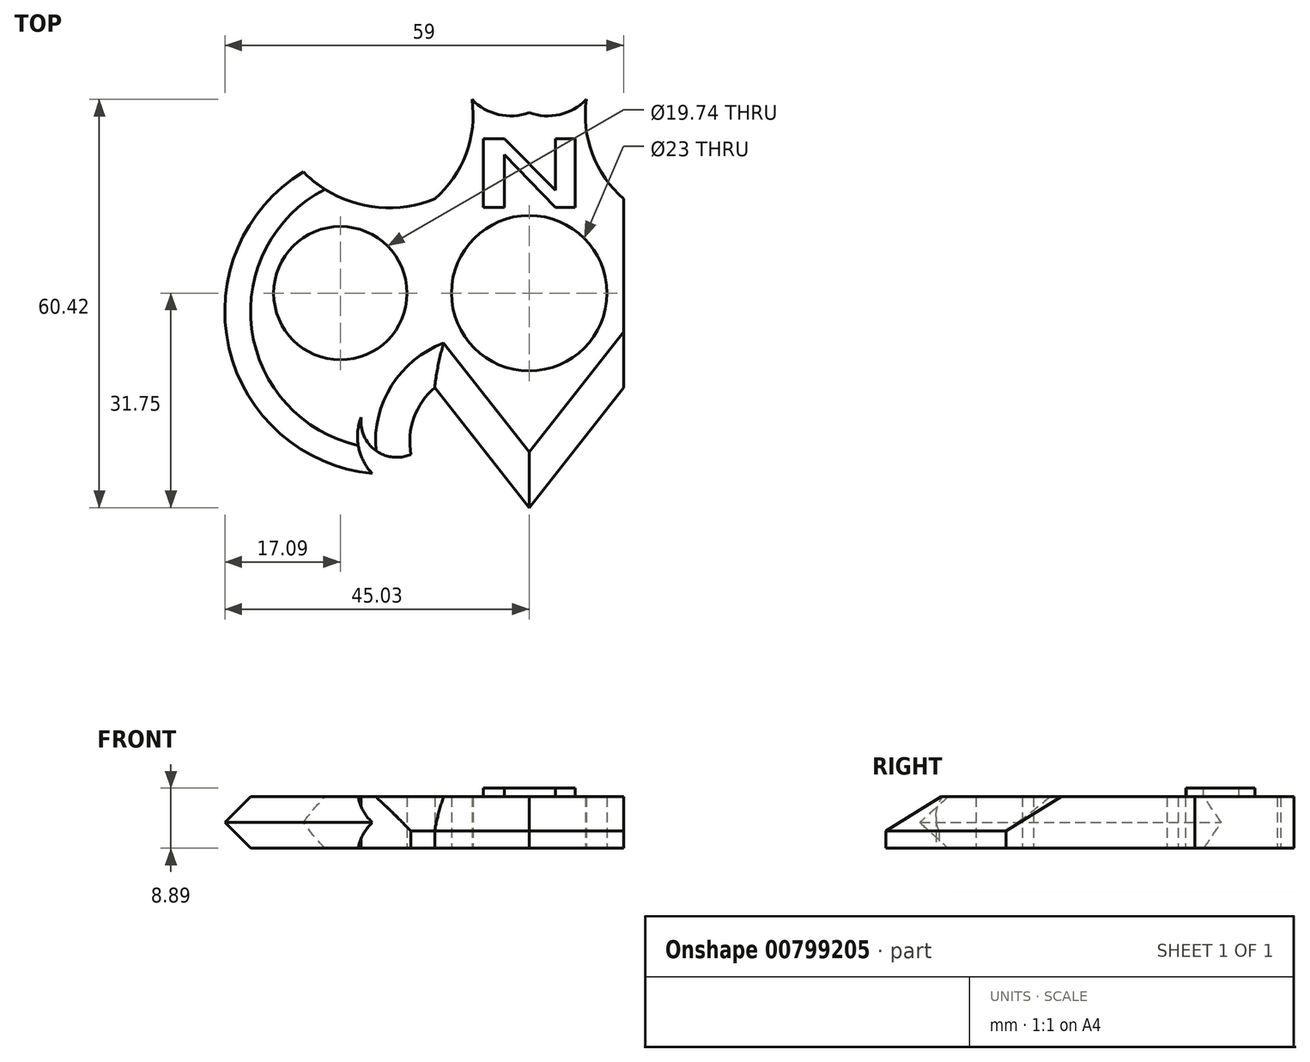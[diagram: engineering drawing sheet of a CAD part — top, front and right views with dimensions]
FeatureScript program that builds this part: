
annotation { "Feature Type Name" : "Feature", "Feature Type Description" : "" }
export const myFeature = defineFeature(function(context is Context, id is Id, definition is map)
    precondition{}
    {
        {
            var Q0;
            Q0=qCreatedBy(makeId("Top.planeOp"),FACE);
            var sketch = newSketch(context, id + "F0", { "sketchPlane" : qUnion([Q0])});
            skCircle(sketch, "E0", {"center": v(0, 0) * mm, "radius": 11.5 * mm});
            skLineSegment(sketch, "E1.bottom", {"start": v(13.97, -13.97) * mm, "end": v(-13.97, -13.97) * mm});
            skLineSegment(sketch, "E1.top", {"start": v(13.97, 13.97) * mm, "end": v(-13.97, 13.97) * mm});
            skLineSegment(sketch, "E1.left", {"start": v(13.97, -13.97) * mm, "end": v(13.97, 13.97) * mm});
            skLineSegment(sketch, "E1.right", {"start": v(-13.97, -13.97) * mm, "end": v(-13.97, 13.97) * mm});
            skArc(sketch, "E2", {"start": v(-34.3, 18.9) * mm, "mid": v(-24.93, 13.13) * mm, "end": v(-13.97, 13.97) * mm});
            skArc(sketch, "E3", {"start": v(-34.3, 18.9) * mm, "mid": v(-45.4, -9.38) * mm, "end": v(-21.46, -28.08) * mm});
            skLineSegment(sketch, "E4", {"start": v(-13.97, -13.97) * mm, "end": v(0, -31.75) * mm});
            skArc(sketch, "E5", {"start": v(-13.97, 13.97) * mm, "mid": v(-9.35, 20.62) * mm, "end": v(-8.45, 28.67) * mm});
            skArc(sketch, "E6", {"start": v(-8.45, 28.67) * mm, "mid": v(-4.52, 26.42) * mm, "end": v(0, 26.71) * mm});
            skLineSegment(sketch, "E7.MirrorCS", {"start": v(13.97, -13.97) * mm, "end": v(0, -31.75) * mm});
            skArc(sketch, "E8.MirrorCS", {"start": v(34.3, 18.9) * mm, "mid": v(24.93, 13.13) * mm, "end": v(13.97, 13.97) * mm});
            skArc(sketch, "E9.MirrorCS", {"start": v(34.3, 18.9) * mm, "mid": v(45.4, -9.38) * mm, "end": v(21.46, -28.08) * mm});
            skArc(sketch, "E10.MirrorCS", {"start": v(8.45, 28.67) * mm, "mid": v(4.52, 26.42) * mm, "end": v(0, 26.71) * mm});
            skArc(sketch, "E11.MirrorCS", {"start": v(13.97, 13.97) * mm, "mid": v(9.35, 20.62) * mm, "end": v(8.45, 28.67) * mm});
            skArc(sketch, "E12", {"start": v(-24.87, -18.38) * mm, "mid": v(-24.96, -23.86) * mm, "end": v(-21.46, -28.08) * mm});
            skArc(sketch, "E13", {"start": v(-24.87, -18.38) * mm, "mid": v(-22.77, -23.25) * mm, "end": v(-17.5, -23.86) * mm});
            skPoint(sketch, "E13.endSnap0", {"position": v(-24.96, -23.86) * mm});
            skArc(sketch, "E14", {"start": v(-13.97, -13.97) * mm, "mid": v(-17.05, -18.44) * mm, "end": v(-17.5, -23.86) * mm});
            skArc(sketch, "E15.MirrorCS", {"start": v(13.97, -13.97) * mm, "mid": v(17.05, -18.44) * mm, "end": v(17.5, -23.86) * mm});
            skPoint(sketch, "E16.MirrorP", {"position": v(24.96, -23.86) * mm});
            skArc(sketch, "E17.MirrorCS", {"start": v(24.87, -18.38) * mm, "mid": v(22.77, -23.25) * mm, "end": v(17.5, -23.86) * mm});
            skArc(sketch, "E18.MirrorCS", {"start": v(24.87, -18.38) * mm, "mid": v(24.96, -23.86) * mm, "end": v(21.46, -28.08) * mm});
            skCircle(sketch, "E19", {"center": v(-27.94, 0) * mm, "radius": 9.87 * mm});
            skCircle(sketch, "E20", {"center": v(27.94, 0) * mm, "radius": 9.87 * mm});
            skSolve(sketch);
        }
        {
            var Q0;
            Q0=makeQuery(id+"F0.imprint","IMPRINT",FACE,{"disambiguationData":[TD([[makeQuery(id+"F0.imprint","IMPRINT",EDGE,{"derivedFrom":sQuery(id+"F0.wireOp",EDGE,"E1.right")}),1.0]])]});
            var Q1;
            Q1=makeQuery(id+"F0.imprint","IMPRINT",FACE,{"disambiguationData":[TD([[makeQuery(id+"F0.imprint","IMPRINT",EDGE,{"derivedFrom":sQuery(id+"F0.wireOp",EDGE,"E1.top")}),-1.0]])]});
            var Q2;
            Q2=makeQuery(id+"F0.imprint","IMPRINT",FACE,{"disambiguationData":[TD([[makeQuery(id+"F0.imprint","IMPRINT",EDGE,{"derivedFrom":sQuery(id+"F0.wireOp",EDGE,"E0")}),-1.0]])]});
            var Q3;
            Q3=makeQuery(id+"F0.imprint","IMPRINT",FACE,{"disambiguationData":[TD([[makeQuery(id+"F0.imprint","IMPRINT",EDGE,{"derivedFrom":sQuery(id+"F0.wireOp",EDGE,"E8.MirrorCS")}),1.0]])]});
            var Q4;
            Q4=makeQuery(id+"F0.imprint","IMPRINT",FACE,{"disambiguationData":[TD([[makeQuery(id+"F0.imprint","IMPRINT",EDGE,{"derivedFrom":sQuery(id+"F0.wireOp",EDGE,"E1.bottom")}),1.0]])]});
            extrude(context, id + "F1", {"entities" : qUnion([Q0, Q1, Q2, Q3, Q4]), "depth" : 7.62 * mm, "offsetDistance" : 25.4 * mm});
        }
        {
            var Q0;
            Q0=makeQuery(id+"F1.opExtrude","CAP_EDGE",EDGE,{"disambiguationData":[OSD([sQuery(id+"F0.wireOp",EDGE,"E4")])],"isStart":false});
            var Q1;
            Q1=makeQuery(id+"F1.opExtrude","CAP_EDGE",EDGE,{"disambiguationData":[OSD([sQuery(id+"F0.wireOp",EDGE,"E7.MirrorCS")])],"isStart":false});
            var Q2;
            Q2=makeQuery(id+"F1.opExtrude","CAP_EDGE",EDGE,{"disambiguationData":[OSD([sQuery(id+"F0.wireOp",EDGE,"E14")])],"isStart":false});
            var Q3;
            Q3=makeQuery(id+"F1.opExtrude","CAP_EDGE",EDGE,{"disambiguationData":[OSD([sQuery(id+"F0.wireOp",EDGE,"E15.MirrorCS")])],"isStart":false});
            var Q4;
            Q4=makeQuery(id+"F1.opExtrude","CAP_EDGE",EDGE,{"disambiguationData":[OSD([sQuery(id+"F0.wireOp",EDGE,"E9.MirrorCS")])],"isStart":false});
            var Q5;
            Q5=makeQuery(id+"F1.opExtrude","CAP_EDGE",EDGE,{"disambiguationData":[OSD([sQuery(id+"F0.wireOp",EDGE,"E3")])],"isStart":false});
            var Q6;
            Q6=makeQuery(id+"F1.opExtrude","CAP_EDGE",EDGE,{"disambiguationData":[OSD([sQuery(id+"F0.wireOp",EDGE,"E3")])],"isStart":true});
            var Q7;
            Q7=makeQuery(id+"F1.opExtrude","CAP_EDGE",EDGE,{"disambiguationData":[OSD([sQuery(id+"F0.wireOp",EDGE,"E9.MirrorCS")])],"isStart":true});
            chamfer(context, id + "F2", {"entities" : qUnion([Q0, Q1, Q2, Q3, Q4, Q5, Q6, Q7]), "width" : 5.08 * mm, "tangentPropagation" : true});
        }
        {
            var Q0;
            Q0=makeQuery(id+"F1.opExtrude","CAP_FACE",FACE,{"disambiguationData":[OSD([sQuery(id+"F0.wireOp",EDGE,"E0"),sQuery(id+"F0.wireOp",EDGE,"E2"),sQuery(id+"F0.wireOp",EDGE,"E3"),sQuery(id+"F0.wireOp",EDGE,"E4"),sQuery(id+"F0.wireOp",EDGE,"E5"),sQuery(id+"F0.wireOp",EDGE,"E6"),sQuery(id+"F0.wireOp",EDGE,"E7.MirrorCS"),sQuery(id+"F0.wireOp",EDGE,"E8.MirrorCS"),sQuery(id+"F0.wireOp",EDGE,"E9.MirrorCS"),sQuery(id+"F0.wireOp",EDGE,"E10.MirrorCS"),sQuery(id+"F0.wireOp",EDGE,"E11.MirrorCS"),sQuery(id+"F0.wireOp",EDGE,"E12"),sQuery(id+"F0.wireOp",EDGE,"E13"),sQuery(id+"F0.wireOp",EDGE,"E14"),sQuery(id+"F0.wireOp",EDGE,"E15.MirrorCS"),sQuery(id+"F0.wireOp",EDGE,"E17.MirrorCS"),sQuery(id+"F0.wireOp",EDGE,"E18.MirrorCS"),sQuery(id+"F0.wireOp",EDGE,"E19"),sQuery(id+"F0.wireOp",EDGE,"E20")])],"isStart":false});
            var sketch = newSketch(context, id + "F3", { "sketchPlane" : qUnion([Q0])});
            skPoint(sketch, "E21.oppositeSnap0", {"position": v(-22.27, 12.7) * mm});
            skLineSegment(sketch, "E21.bottom", {"start": v(-6.8, 22.86) * mm, "end": v(-3.68, 22.86) * mm});
            skLineSegment(sketch, "E21.top", {"start": v(-6.8, 12.7) * mm, "end": v(-3.68, 12.7) * mm});
            skLineSegment(sketch, "E21.left", {"start": v(-6.8, 22.86) * mm, "end": v(-6.8, 12.7) * mm});
            skLineSegment(sketch, "E21.right", {"start": v(-3.68, 22.86) * mm, "end": v(-3.68, 12.7) * mm});
            skLineSegment(sketch, "E22.bottom", {"start": v(3.86, 22.87) * mm, "end": v(6.8, 22.87) * mm});
            skLineSegment(sketch, "E22.top", {"start": v(3.86, 12.7) * mm, "end": v(6.8, 12.7) * mm});
            skLineSegment(sketch, "E22.left", {"start": v(3.86, 22.87) * mm, "end": v(3.86, 12.7) * mm});
            skLineSegment(sketch, "E22.right", {"start": v(6.8, 22.87) * mm, "end": v(6.8, 12.7) * mm});
            skLineSegment(sketch, "E23", {"start": v(-3.68, 22.86) * mm, "end": v(3.86, 15.23) * mm});
            skLineSegment(sketch, "E24", {"start": v(3.86, 12.7) * mm, "end": v(-3.68, 20.49) * mm});
            skSolve(sketch);
        }
        {
            var Q0;
            Q0 = qSketchRegion(id + "F3", true);
            extrude(context, id + "F4", {"entities" : qUnion([Q0]), "operationType" : NewBodyOperationType.ADD, "depth" : 1.27 * mm, "offsetDistance" : 25.4 * mm});
        }
    });
